# Revit family: Lighting_Device-Count_Down_Timer-Hubbell_Wiring-DT5030W
name_source: partatom
category: Lighting Devices
revit_build: Autodesk Revit 2015 (Build: 20140606_1530(x64)
units: mm (PartAtom-declared; Revit-internal decimal feet)

## types (3) — shared parameters
Certifications = cULus listed to UL60730-1 and UL60730-2
Connector Description 1 = Power Supply
Connector Description 2 = Controls
Default Elevation = 48 "
Description = Count Down Timer Wall Switch Timers
Frequency = 60 Hz
Housing Material = Plastic - Hubbell - Black
Humidity = 0% to 95% relative humidity, non-condensing
Load Classification = Lighting
Manufacturer = Hubbell Wiring Device-Kellems
Model = DT5030W
Number of Poles = 1
Operating Temperature = 32° – 104°F (0° – 40°C)
Power Factor = 1
Product Documentation Link = http://ecatalog.hubbell-wiring.com
Product data url = https://bimobject.com
Time Delay = 5, 10, 20, 30 minutes
URL = http://www.hubbell-wiring.com

## per-type parameters (varying)
| type | Product Material | Product Page URL | UPC Number |
| DT-White | Plastic - Hubbell - White | http://ecatalog.hubbell-wiring.com
http://ecatalog.hubbell-wiring.com | 783585256412 |
| DT-Ivory | Plastic - Hubbell - Ivory | http://ecatalog.hubbell-wiring.com | 783585256405 |
| DT-Light Almond | Plastic - Hubbell - Light Almond | http://ecatalog.hubbell-wiring.com | 783585256399 |

## geometry (parser evidence)
native form markers: Blend x12, Sweep x1
no freeform markers — native parametric forms only
